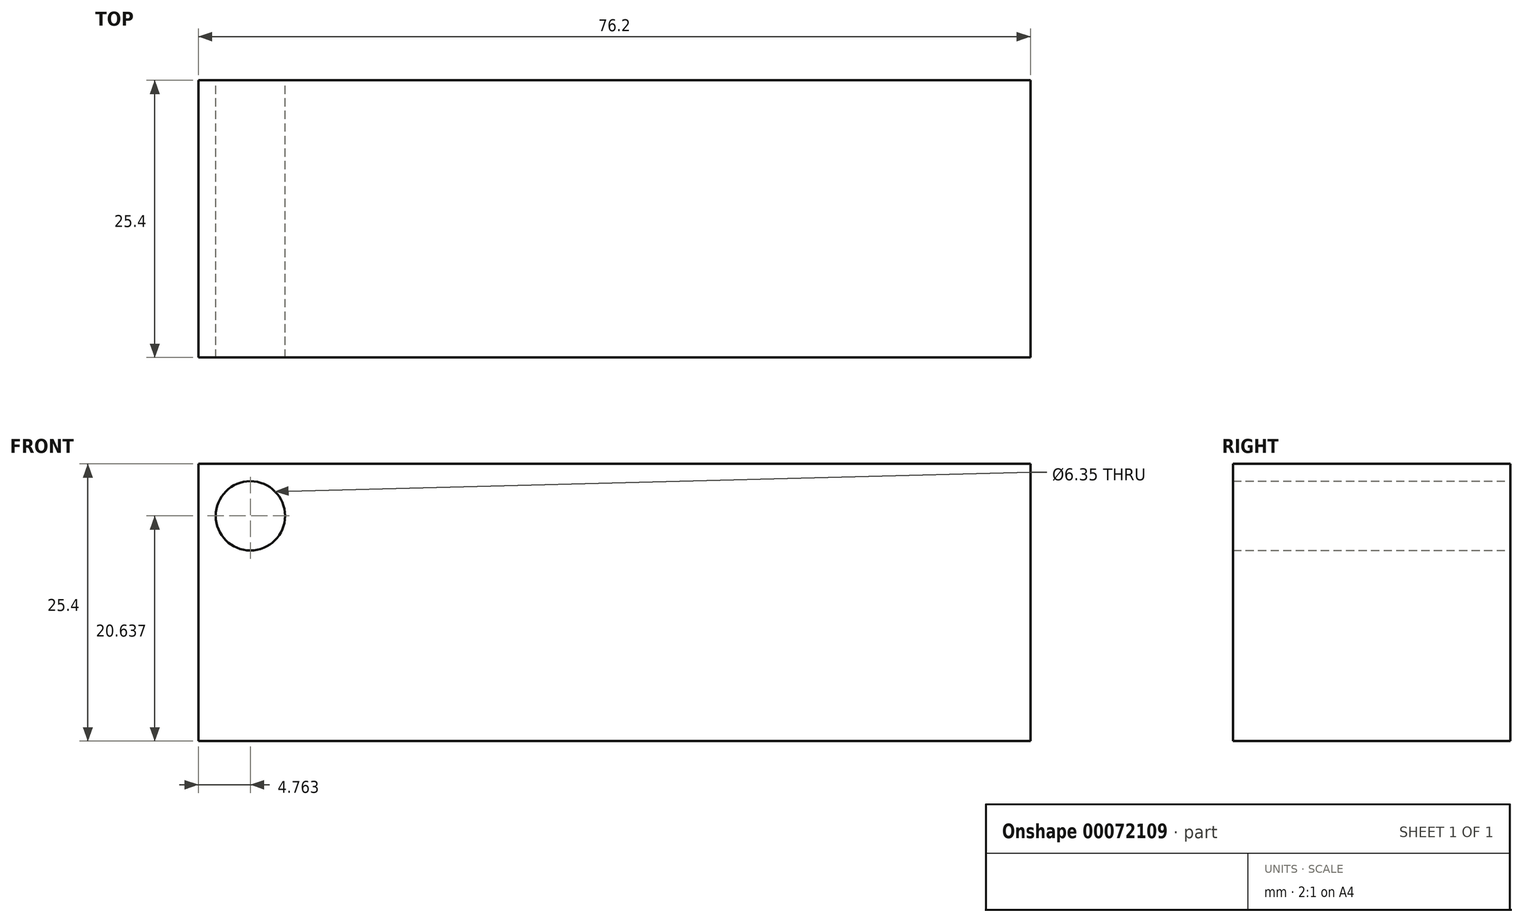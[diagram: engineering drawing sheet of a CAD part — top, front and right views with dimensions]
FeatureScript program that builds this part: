
annotation { "Feature Type Name" : "Feature", "Feature Type Description" : "" }
export const myFeature = defineFeature(function(context is Context, id is Id, definition is map)
    precondition{}
    {
        {
            var Q0;
            Q0=qCreatedBy(makeId("Front.planeOp"),FACE);
            var sketch = newSketch(context, id + "F0", { "sketchPlane" : qUnion([Q0])});
            skLineSegment(sketch, "E0.bottom", {"start": v(0, 0) * mm, "end": v(76.2, 0) * mm});
            skLineSegment(sketch, "E0.top", {"start": v(0, 25.4) * mm, "end": v(76.2, 25.4) * mm});
            skLineSegment(sketch, "E0.left", {"start": v(0, 0) * mm, "end": v(0, 25.4) * mm});
            skLineSegment(sketch, "E0.right", {"start": v(76.2, 0) * mm, "end": v(76.2, 25.4) * mm});
            skCircle(sketch, "E1", {"center": v(4.76, 20.64) * mm, "radius": 3.18 * mm});
            skSolve(sketch);
        }
        {
            var Q0;
            Q0=makeQuery(id+"F0.imprint","IMPRINT",FACE,{"disambiguationData":[TD([[makeQuery(id+"F0.imprint","IMPRINT",EDGE,{"derivedFrom":sQuery(id+"F0.wireOp",EDGE,"E0.bottom")}),1.0]])]});
            extrude(context, id + "F1", {"entities" : qUnion([Q0]), "depth" : 25.4 * mm});
        }
    });
